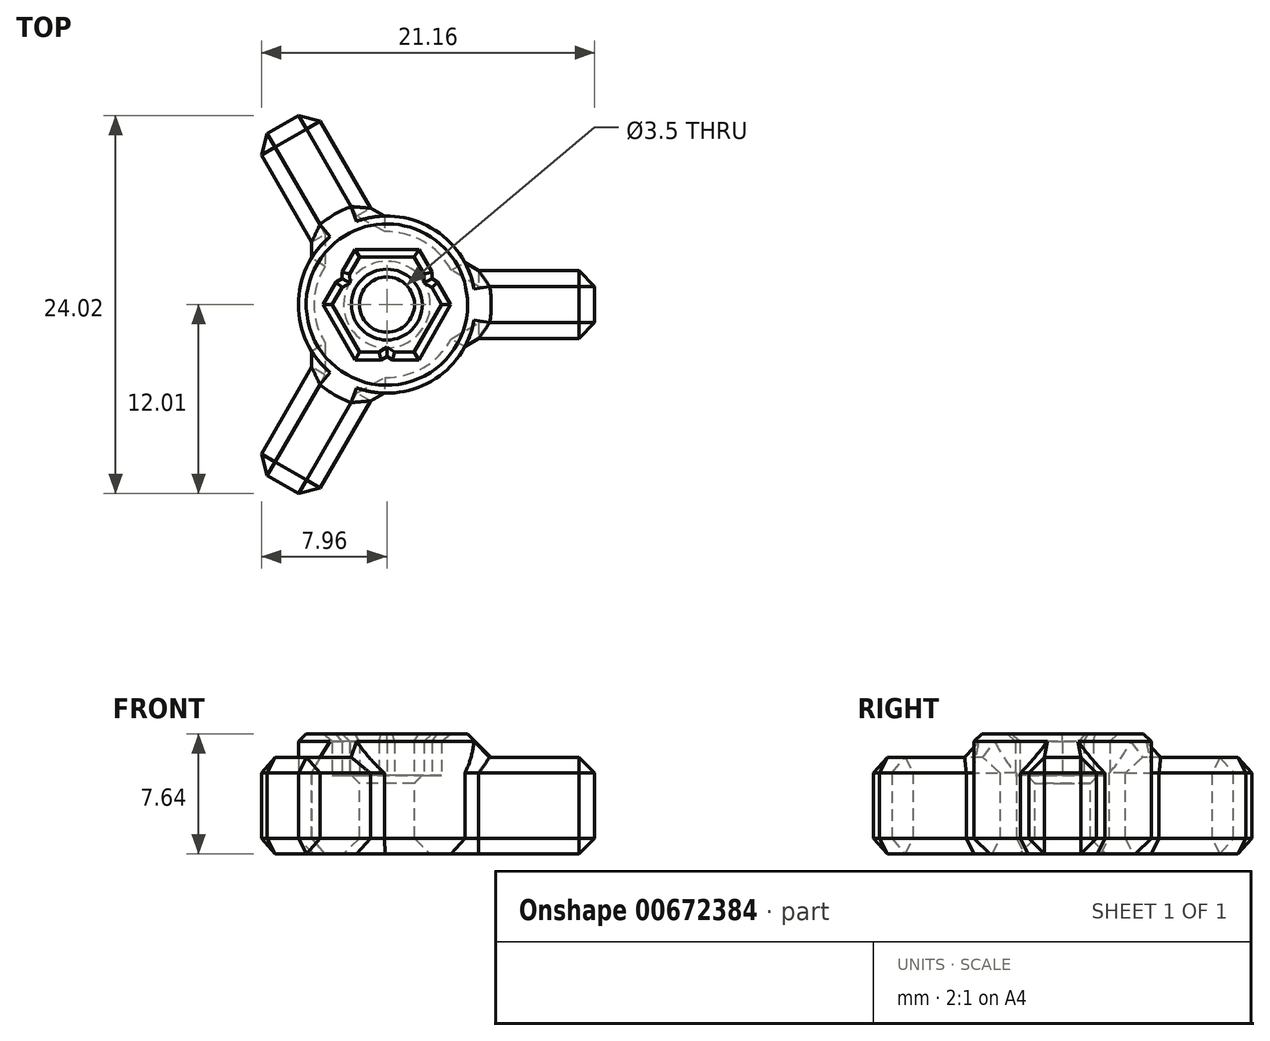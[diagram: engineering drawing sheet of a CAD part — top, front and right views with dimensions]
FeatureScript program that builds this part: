
annotation { "Feature Type Name" : "Feature", "Feature Type Description" : "" }
export const myFeature = defineFeature(function(context is Context, id is Id, definition is map)
    precondition{}
    {
        {
            assignVariable(context, id + "F0", {"name" : "d", "anyValue" : 3.3});
        }
        {
            assignVariable(context, id + "F1", {"name" : "m", "anyValue" : getVariable(context, 'd') * 0.8});
        }
        {
            var Q0;
            Q0=qCreatedBy(makeId("Top.planeOp"),FACE);
            var sketch = newSketch(context, id + "F2", { "sketchPlane" : qUnion([Q0])});
            skLineSegment(sketch, "E0", {"start": v(13.2, 0) * mm, "end": v(0, 0) * mm, "construction": true});
            skLineSegment(sketch, "E1", {"start": v(13.2, 2.15) * mm, "end": v(13.2, -2.15) * mm});
            skLineSegment(sketch, "E2", {"start": v(13.2, -2.15) * mm, "end": v(5.2, -2.15) * mm});
            skLineSegment(sketch, "E3", {"start": v(13.2, 2.15) * mm, "end": v(5.2, 2.15) * mm});
            skPoint(sketch, "E4.center", {"position": v(0, 0) * mm});
            skCircle(sketch, "E5.cCircle", {"center": v(0, 0) * mm, "radius": 3 * mm, "construction": true});
            skLineSegment(sketch, "E5.0", {"start": v(-1.74, 3) * mm, "end": v(1.74, 3) * mm});
            skLineSegment(sketch, "E5.2", {"start": v(3.48, 0) * mm, "end": v(1.74, -3.01) * mm});
            skLineSegment(sketch, "E5.3", {"start": v(1.74, -3) * mm, "end": v(0.5, -3) * mm});
            skLineSegment(sketch, "E5.4", {"start": v(-1.74, -3) * mm, "end": v(-3.48, 0) * mm});
            skPoint(sketch, "E5.0.midPoint", {"position": v(0, 3) * mm});
            skCircle(sketch, "E6.cCircle", {"center": v(0, 0) * mm, "radius": 5.63 * mm});
            skLineSegment(sketch, "E7.1.0", {"start": v(-8.46, 10.36) * mm, "end": v(-4.46, 3.43) * mm});
            skLineSegment(sketch, "E7.1.1", {"start": v(-8.46, 10.36) * mm, "end": v(-4.74, 12.5) * mm});
            skLineSegment(sketch, "E7.1.2", {"start": v(-4.74, 12.5) * mm, "end": v(-0.74, 5.58) * mm});
            skLineSegment(sketch, "E7.1.3", {"start": v(-6.6, 11.43) * mm, "end": v(0, 0) * mm, "construction": true});
            skLineSegment(sketch, "E7.2.0", {"start": v(-4.74, -12.5) * mm, "end": v(-0.74, -5.58) * mm});
            skLineSegment(sketch, "E7.2.1", {"start": v(-4.74, -12.5) * mm, "end": v(-8.46, -10.36) * mm});
            skLineSegment(sketch, "E7.2.2", {"start": v(-8.46, -10.36) * mm, "end": v(-4.46, -3.43) * mm});
            skLineSegment(sketch, "E7.2.3", {"start": v(-6.6, -11.43) * mm, "end": v(0, 0) * mm, "construction": true});
            skCircle(sketch, "E8", {"center": v(0, 0) * mm, "radius": 1.75 * mm});
            skLineSegment(sketch, "E9", {"start": v(0.5, -3) * mm, "end": v(0, -2.7) * mm});
            skLineSegment(sketch, "E10", {"start": v(0, -2.7) * mm, "end": v(-0.5, -3) * mm});
            skLineSegment(sketch, "E11.trimOffspring", {"start": v(-0.5, -3) * mm, "end": v(-1.74, -3) * mm});
            skLineSegment(sketch, "E12.1.0", {"start": v(2.86, 1.07) * mm, "end": v(3.48, 0) * mm});
            skLineSegment(sketch, "E12.1.1", {"start": v(2.35, 1.35) * mm, "end": v(2.86, 1.07) * mm});
            skLineSegment(sketch, "E12.1.2", {"start": v(2.36, 1.94) * mm, "end": v(2.35, 1.35) * mm});
            skLineSegment(sketch, "E12.1.3", {"start": v(1.74, 3) * mm, "end": v(2.36, 1.94) * mm});
            skLineSegment(sketch, "E12.2.0", {"start": v(-2.36, 1.94) * mm, "end": v(-1.74, 3.01) * mm});
            skLineSegment(sketch, "E12.2.1", {"start": v(-2.35, 1.35) * mm, "end": v(-2.36, 1.94) * mm});
            skLineSegment(sketch, "E12.2.2", {"start": v(-2.86, 1.07) * mm, "end": v(-2.35, 1.35) * mm});
            skLineSegment(sketch, "E12.2.3", {"start": v(-3.48, 0) * mm, "end": v(-2.86, 1.07) * mm});
            skSolve(sketch);
        }
        {
            var Q0;
            Q0=makeQuery(id+"F2.imprint","IMPRINT",FACE,{"disambiguationData":[TD([[makeQuery(id+"F2.imprint","IMPRINT",EDGE,{"derivedFrom":sQuery(id+"F2.wireOp",EDGE,"E5.0")}),1.0]])]});
            extrude(context, id + "F3", {"entities" : qUnion([Q0]), "depth" : (getVariable(context, 'm')) * mm, "offsetDistance" : 25 * mm});
        }
        {
            var Q0;
            Q0 = qSketchRegion(id + "F2", true);
            var Q1;
            Q1=makeQuery(id+"F2.imprint","IMPRINT",FACE,{"disambiguationData":[TD([[makeQuery(id+"F2.imprint","IMPRINT",EDGE,{"derivedFrom":sQuery(id+"F2.wireOp",EDGE,"E5.0")}),-1.0]])]});
            extrude(context, id + "F4", {"entities" : qUnion([Q0, Q1]), "operationType" : NewBodyOperationType.ADD, "oppositeDirection" : true, "depth" : 5 * mm, "offsetDistance" : 25 * mm});
        }
        {
            var Q0;
            Q0 = qSketchRegion(id + "F2", true);
            extrude(context, id + "F5", {"entities" : qUnion([Q0]), "operationType" : NewBodyOperationType.ADD, "depth" : (getVariable(context, 'm') - 1.5) * mm, "offsetDistance" : 25 * mm});
        }
        {
            var Q0;
            Q0=makeQuery(id+"F3.opExtrude","CAP_FACE",FACE,{"disambiguationData":[OSD([sQuery(id+"F2.wireOp",EDGE,"E5.0"),sQuery(id+"F2.wireOp",EDGE,"E5.1"),sQuery(id+"F2.wireOp",EDGE,"E5.2"),sQuery(id+"F2.wireOp",EDGE,"E5.3"),sQuery(id+"F2.wireOp",EDGE,"E5.4"),sQuery(id+"F2.wireOp",EDGE,"E5.5"),sQuery(id+"F2.wireOp",EDGE,"E6.0"),sQuery(id+"F2.wireOp",EDGE,"E6.1"),sQuery(id+"F2.wireOp",EDGE,"E6.2"),sQuery(id+"F2.wireOp",EDGE,"E6.3"),sQuery(id+"F2.wireOp",EDGE,"E6.4"),sQuery(id+"F2.wireOp",EDGE,"E6.5"),sQuery(id+"F2.wireOp",EDGE,"E6.6"),sQuery(id+"F2.wireOp",EDGE,"E6.7")])],"isStart":false});
            var Q1;
            Q1=makeQuery(id+"F4.opExtrude","CAP_EDGE",EDGE,{"disambiguationData":[OSD([sQuery(id+"F2.wireOp",EDGE,"E8")])],"isStart":true});
            chamfer(context, id + "F6", {"entities" : qUnion([Q0, Q1]), "width" : 0.5 * mm, "tangentPropagation" : true});
        }
        {
            var Q0;
            Q0=makeQuery(id+"F4.opExtrude","CAP_FACE",FACE,{"disambiguationData":[OSD([sQuery(id+"F2.wireOp",EDGE,"E1"),sQuery(id+"F2.wireOp",EDGE,"E2"),sQuery(id+"F2.wireOp",EDGE,"E3"),sQuery(id+"F2.wireOp",EDGE,"E6.0"),sQuery(id+"F2.wireOp",EDGE,"E6.1"),sQuery(id+"F2.wireOp",EDGE,"E6.2"),sQuery(id+"F2.wireOp",EDGE,"E6.3"),sQuery(id+"F2.wireOp",EDGE,"E6.4"),sQuery(id+"F2.wireOp",EDGE,"E6.5"),sQuery(id+"F2.wireOp",EDGE,"E6.6"),sQuery(id+"F2.wireOp",EDGE,"E6.7"),sQuery(id+"F2.wireOp",EDGE,"E7.1.0"),sQuery(id+"F2.wireOp",EDGE,"E7.1.1"),sQuery(id+"F2.wireOp",EDGE,"E7.1.2"),sQuery(id+"F2.wireOp",EDGE,"E7.2.0"),sQuery(id+"F2.wireOp",EDGE,"E7.2.1"),sQuery(id+"F2.wireOp",EDGE,"E7.2.2"),sQuery(id+"F2.wireOp",EDGE,"E7.3.0"),sQuery(id+"F2.wireOp",EDGE,"E7.3.1"),sQuery(id+"F2.wireOp",EDGE,"E7.3.2"),sQuery(id+"F2.wireOp",EDGE,"E7.4.0"),sQuery(id+"F2.wireOp",EDGE,"E7.4.1"),sQuery(id+"F2.wireOp",EDGE,"E7.4.2"),sQuery(id+"F2.wireOp",EDGE,"E7.5.0"),sQuery(id+"F2.wireOp",EDGE,"E7.5.1"),sQuery(id+"F2.wireOp",EDGE,"E7.5.2"),sQuery(id+"F2.wireOp",EDGE,"E7.6.0"),sQuery(id+"F2.wireOp",EDGE,"E7.6.1"),sQuery(id+"F2.wireOp",EDGE,"E7.6.2"),sQuery(id+"F2.wireOp",EDGE,"E7.7.0"),sQuery(id+"F2.wireOp",EDGE,"E7.7.1"),sQuery(id+"F2.wireOp",EDGE,"E7.7.2")])],"isStart":false});
            var Q1;
            {var subQ0=sQuery(id+"F2.wireOp",EDGE,"E7.3.1");Q1=makeQuery(id+"F5.boolean.opBoolean","MERGE",FACE,{"derivedFrom":[makeQuery(id+"F4.opExtrude","SWEPT_FACE",FACE,{"disambiguationData":[OSD([subQ0])]}),makeQuery(id+"F5.opExtrude","SWEPT_FACE",FACE,{"disambiguationData":[OSD([subQ0])]})]});}
            var Q2;
            {var subQ0=sQuery(id+"F2.wireOp",EDGE,"E7.4.1");Q2=makeQuery(id+"F5.boolean.opBoolean","MERGE",FACE,{"derivedFrom":[makeQuery(id+"F4.opExtrude","SWEPT_FACE",FACE,{"disambiguationData":[OSD([subQ0])]}),makeQuery(id+"F5.opExtrude","SWEPT_FACE",FACE,{"disambiguationData":[OSD([subQ0])]})]});}
            var Q3;
            {var subQ0=sQuery(id+"F2.wireOp",EDGE,"E7.5.1");Q3=makeQuery(id+"F5.boolean.opBoolean","MERGE",FACE,{"derivedFrom":[makeQuery(id+"F4.opExtrude","SWEPT_FACE",FACE,{"disambiguationData":[OSD([subQ0])]}),makeQuery(id+"F5.opExtrude","SWEPT_FACE",FACE,{"disambiguationData":[OSD([subQ0])]})]});}
            var Q4;
            {var subQ0=sQuery(id+"F2.wireOp",EDGE,"E7.6.1");Q4=makeQuery(id+"F5.boolean.opBoolean","MERGE",FACE,{"derivedFrom":[makeQuery(id+"F4.opExtrude","SWEPT_FACE",FACE,{"disambiguationData":[OSD([subQ0])]}),makeQuery(id+"F5.opExtrude","SWEPT_FACE",FACE,{"disambiguationData":[OSD([subQ0])]})]});}
            var Q5;
            {var subQ0=sQuery(id+"F2.wireOp",EDGE,"E7.7.1");Q5=makeQuery(id+"F5.boolean.opBoolean","MERGE",FACE,{"derivedFrom":[makeQuery(id+"F4.opExtrude","SWEPT_FACE",FACE,{"disambiguationData":[OSD([subQ0])]}),makeQuery(id+"F5.opExtrude","SWEPT_FACE",FACE,{"disambiguationData":[OSD([subQ0])]})]});}
            var Q6;
            {var subQ0=sQuery(id+"F2.wireOp",EDGE,"E1");Q6=makeQuery(id+"F5.boolean.opBoolean","MERGE",FACE,{"derivedFrom":[makeQuery(id+"F4.opExtrude","SWEPT_FACE",FACE,{"disambiguationData":[OSD([subQ0])]}),makeQuery(id+"F5.opExtrude","SWEPT_FACE",FACE,{"disambiguationData":[OSD([subQ0])]})]});}
            var Q7;
            {var subQ0=sQuery(id+"F2.wireOp",EDGE,"E7.1.1");Q7=makeQuery(id+"F5.boolean.opBoolean","MERGE",FACE,{"derivedFrom":[makeQuery(id+"F4.opExtrude","SWEPT_FACE",FACE,{"disambiguationData":[OSD([subQ0])]}),makeQuery(id+"F5.opExtrude","SWEPT_FACE",FACE,{"disambiguationData":[OSD([subQ0])]})]});}
            var Q8;
            {var subQ0=sQuery(id+"F2.wireOp",EDGE,"E7.2.1");Q8=makeQuery(id+"F5.boolean.opBoolean","MERGE",FACE,{"derivedFrom":[makeQuery(id+"F4.opExtrude","SWEPT_FACE",FACE,{"disambiguationData":[OSD([subQ0])]}),makeQuery(id+"F5.opExtrude","SWEPT_FACE",FACE,{"disambiguationData":[OSD([subQ0])]})]});}
            var Q9;
            {var subQ0=sQuery(id+"F2.wireOp",EDGE,"E6.cCircle");var subQ1=sQuery(id+"F2.wireOp",EDGE,"E2");var subQ2=sQuery(id+"F2.wireOp",EDGE,"E7.2.0");var subQ3=sQuery(id+"F2.wireOp",EDGE,"E7.1.0");var subQ4=sQuery(id+"F2.wireOp",EDGE,"E7.2.2");var subQ5=sQuery(id+"F2.wireOp",EDGE,"E3");var subQ6=sQuery(id+"F2.wireOp",EDGE,"E7.1.2");var subQ7=sQuery(id+"F2.wireOp",EDGE,"E7.1.1");Q9=makeQuery(id+"F5.boolean.opBoolean","SPLIT",FACE,{"disambiguationData":[TD([makeQuery(id+"F4.opExtrude","SWEPT_FACE",FACE,{"disambiguationData":[OSD([subQ3])]})])],"derivedFrom":makeQuery(id+"F5.opExtrude","CAP_FACE",FACE,{"disambiguationData":[OSD([sQuery(id+"F2.wireOp",EDGE,"E1"),subQ1,subQ5,sQuery(id+"F2.wireOp",EDGE,"E5.0"),sQuery(id+"F2.wireOp",EDGE,"E5.1"),sQuery(id+"F2.wireOp",EDGE,"E5.2"),sQuery(id+"F2.wireOp",EDGE,"E5.3"),sQuery(id+"F2.wireOp",EDGE,"E5.4"),sQuery(id+"F2.wireOp",EDGE,"E5.5"),subQ0,subQ3,subQ7,subQ6,subQ2,sQuery(id+"F2.wireOp",EDGE,"E7.2.1"),subQ4])],"isStart":false})});}
            var Q10;
            {var subQ0=sQuery(id+"F2.wireOp",EDGE,"E3");var subQ1=sQuery(id+"F2.wireOp",EDGE,"E6.cCircle");var subQ2=sQuery(id+"F2.wireOp",EDGE,"E2");var subQ3=sQuery(id+"F2.wireOp",EDGE,"E1");var subQ4=sQuery(id+"F2.wireOp",EDGE,"E7.1.0");var subQ5=sQuery(id+"F2.wireOp",EDGE,"E7.2.2");var subQ6=sQuery(id+"F2.wireOp",EDGE,"E7.2.0");var subQ7=sQuery(id+"F2.wireOp",EDGE,"E7.1.2");Q10=makeQuery(id+"F5.boolean.opBoolean","SPLIT",FACE,{"disambiguationData":[TD([makeQuery(id+"F4.opExtrude","SWEPT_FACE",FACE,{"disambiguationData":[OSD([subQ3])]})])],"derivedFrom":makeQuery(id+"F5.opExtrude","CAP_FACE",FACE,{"disambiguationData":[OSD([subQ3,subQ2,subQ0,sQuery(id+"F2.wireOp",EDGE,"E5.0"),sQuery(id+"F2.wireOp",EDGE,"E5.1"),sQuery(id+"F2.wireOp",EDGE,"E5.2"),sQuery(id+"F2.wireOp",EDGE,"E5.3"),sQuery(id+"F2.wireOp",EDGE,"E5.4"),sQuery(id+"F2.wireOp",EDGE,"E5.5"),subQ1,subQ4,sQuery(id+"F2.wireOp",EDGE,"E7.1.1"),subQ7,subQ6,sQuery(id+"F2.wireOp",EDGE,"E7.2.1"),subQ5])],"isStart":false})});}
            var Q11;
            {var subQ0=sQuery(id+"F2.wireOp",EDGE,"E6.cCircle");var subQ1=sQuery(id+"F2.wireOp",EDGE,"E2");var subQ2=sQuery(id+"F2.wireOp",EDGE,"E7.2.0");var subQ3=sQuery(id+"F2.wireOp",EDGE,"E7.1.0");var subQ4=sQuery(id+"F2.wireOp",EDGE,"E7.2.2");var subQ5=sQuery(id+"F2.wireOp",EDGE,"E3");var subQ6=sQuery(id+"F2.wireOp",EDGE,"E7.1.2");var subQ7=sQuery(id+"F2.wireOp",EDGE,"E7.2.1");Q11=makeQuery(id+"F5.boolean.opBoolean","SPLIT",FACE,{"disambiguationData":[TD([makeQuery(id+"F4.opExtrude","SWEPT_FACE",FACE,{"disambiguationData":[OSD([subQ2])]})])],"derivedFrom":makeQuery(id+"F5.opExtrude","CAP_FACE",FACE,{"disambiguationData":[OSD([sQuery(id+"F2.wireOp",EDGE,"E1"),subQ1,subQ5,sQuery(id+"F2.wireOp",EDGE,"E5.0"),sQuery(id+"F2.wireOp",EDGE,"E5.1"),sQuery(id+"F2.wireOp",EDGE,"E5.2"),sQuery(id+"F2.wireOp",EDGE,"E5.3"),sQuery(id+"F2.wireOp",EDGE,"E5.4"),sQuery(id+"F2.wireOp",EDGE,"E5.5"),subQ0,subQ3,sQuery(id+"F2.wireOp",EDGE,"E7.1.1"),subQ6,subQ2,subQ7,subQ4])],"isStart":false})});}
            chamfer(context, id + "F7", {"entities" : qUnion([Q0, Q1, Q2, Q3, Q4, Q5, Q6, Q7, Q8, Q9, Q10, Q11]), "width" : 1 * mm, "tangentPropagation" : true});
        }
    });
